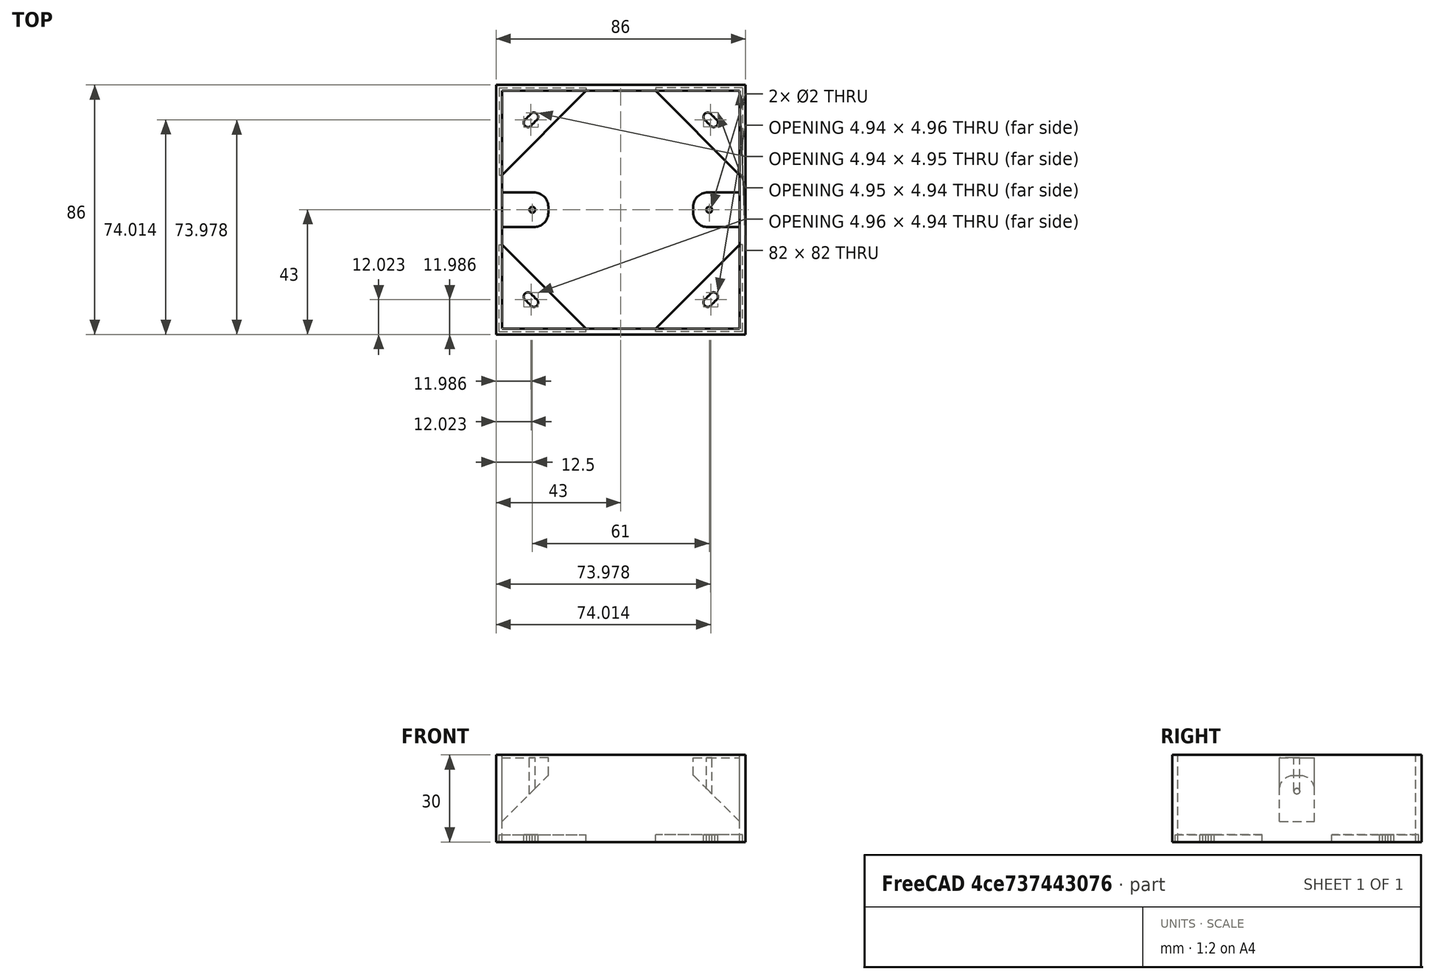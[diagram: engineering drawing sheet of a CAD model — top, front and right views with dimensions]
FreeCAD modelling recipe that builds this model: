
FCSTD DOCUMENT  (FreeCAD 0.16R)
Label: sonoff-aufputz-1v4
License: All rights reserved
LicenseURL: http://en.wikipedia.org/wiki/All_rights_reserved
objects: Part::Cut×19, Part::Cylinder×14, Part::Box×12, Part::Chamfer×6, Part::Fillet×2
note: 53 computed .brp shape members not serialized (recipe doc carries the construction recipe); baked Part::Feature solids carry a one-line shape summary decoded from their .brp

FEATURE [Part::Box] Box  label="Cube"
  Height = 30
  Length = 86
  Width = 86
FEATURE [Part::Box] Box001  label="Cube001"
  Height = 30
  Length = 82
  Placement = pos=(2,2,0) rot=(0,0,1;0rad)
  Width = 82
FEATURE [Part::Cut] Cut
  Base = -> Box
  Tool = -> Box001
FEATURE [Part::Box] Box002  label="Cube002"
  Height = 29
  Length = 16
  Placement = pos=(2,37,0) rot=(0,0,1;0rad)
  Width = 12
FEATURE [Part::Box] Box003  label="Cube003"
  Height = 29
  Length = 16
  Placement = pos=(68,37,0) rot=(0,0,1;0rad)
  Width = 12
FEATURE [Part::Fillet] Fillet  label="Aufnahme1"
  Base = -> Box002
  Edges = 2 edges r=5: [Edge5,Edge7]
FEATURE [Part::Fillet] Fillet001  label="Aufnahme2"
  Base = -> Box003
  Edges = 2 edges r=5: [Edge1,Edge3]
FEATURE [Part::Cylinder] Cylinder  label="Loch1"
  Angle = 360
  Height = 29
  Placement = pos=(12.5,43,0) rot=(0,0,1;0rad)
  Radius = 1
FEATURE [Part::Cylinder] Cylinder001  label="Loch2"
  Angle = 360
  Height = 29
  Placement = pos=(73.5,43,0) rot=(0,0,1;0rad)
  Radius = 1
FEATURE [Part::Cut] Cut001
  Base = -> Fillet
  Tool = -> Cylinder
FEATURE [Part::Cut] Cut002
  Base = -> Fillet001
  Tool = -> Cylinder001
FEATURE [Part::Box] Box009  label="Cube009"
  Height = 2.5
  Length = 30
  Placement = pos=(0,-40,0) rot=(0,0,1;0rad)
  Width = 30
FEATURE [Part::Chamfer] Chamfer004
  Base = -> Box009
  Edges = 1 edges r=29: [Edge7]
FEATURE [Part::Cylinder] Cylinder002  label="Cylinder"
  Angle = 360
  Height = 2.5
  Placement = pos=(10,-28,0) rot=(0,0,1;0rad)
  Radius = 1.5
FEATURE [Part::Cylinder] Cylinder003  label="Cylinder001"
  Angle = 360
  Height = 2.5
  Placement = pos=(11,-29,0) rot=(0,0,1;0rad)
  Radius = 1.5
FEATURE [Part::Cylinder] Cylinder004  label="Cylinder002"
  Angle = 360
  Height = 2.5
  Placement = pos=(12,-30,0) rot=(0,0,1;0rad)
  Radius = 1.5
FEATURE [Part::Cut] Cut003
  Base = -> Chamfer004
  Tool = -> Cylinder002
FEATURE [Part::Cut] Cut004
  Base = -> Cut003
  Tool = -> Cylinder003
FEATURE [Part::Cut] Cut005
  Base = -> Cut004
  Placement = pos=(45,1,0) rot=(0,0,1;1.5708rad)
  Tool = -> Cylinder004
FEATURE [Part::Box] Box010  label="Cube010"
  Height = 2.5
  Length = 30
  Placement = pos=(0,-40,0) rot=(0,0,1;0rad)
  Width = 30
FEATURE [Part::Chamfer] Chamfer005
  Base = -> Box010
  Edges = 1 edges r=29: [Edge7]
FEATURE [Part::Cylinder] Cylinder005  label="Cylinder014"
  Angle = 360
  Height = 2.5
  Placement = pos=(10,-28,0) rot=(0,0,1;0rad)
  Radius = 1.5
FEATURE [Part::Cylinder] Cylinder006  label="Cylinder015"
  Angle = 360
  Height = 2.5
  Placement = pos=(11,-29,0) rot=(0,0,1;0rad)
  Radius = 1.5
FEATURE [Part::Cylinder] Cylinder007  label="Cylinder005"
  Angle = 360
  Height = 2.5
  Placement = pos=(12,-30,0) rot=(0,0,1;0rad)
  Radius = 1.5
FEATURE [Part::Cut] Cut006
  Base = -> Chamfer005
  Tool = -> Cylinder005
FEATURE [Part::Cut] Cut007
  Base = -> Cut006
  Tool = -> Cylinder006
FEATURE [Part::Cut] Cut008
  Base = -> Cut007
  Placement = pos=(85,45,0) rot=(0,0,1;3.14159rad)
  Tool = -> Cylinder007
FEATURE [Part::Box] Box011  label="Cube011"
  Height = 2.5
  Length = 30
  Placement = pos=(0,-40,0) rot=(0,0,1;0rad)
  Width = 30
FEATURE [Part::Chamfer] Chamfer006
  Base = -> Box011
  Edges = 1 edges r=29: [Edge7]
FEATURE [Part::Cylinder] Cylinder008  label="Cylinder016"
  Angle = 360
  Height = 2.5
  Placement = pos=(10,-28,0) rot=(0,0,1;0rad)
  Radius = 1.5
FEATURE [Part::Cylinder] Cylinder009  label="Cylinder017"
  Angle = 360
  Height = 2.5
  Placement = pos=(11,-29,0) rot=(0,0,1;0rad)
  Radius = 1.5
FEATURE [Part::Cylinder] Cylinder010  label="Cylinder018"
  Angle = 360
  Height = 2.5
  Placement = pos=(12,-30,0) rot=(0,0,1;0rad)
  Radius = 1.5
FEATURE [Part::Cut] Cut009
  Base = -> Chamfer006
  Tool = -> Cylinder008
FEATURE [Part::Cut] Cut010
  Base = -> Cut009
  Tool = -> Cylinder009
FEATURE [Part::Cut] Cut011
  Base = -> Cut010
  Placement = pos=(41,85,0) rot=(0,0,-1;1.5708rad)
  Tool = -> Cylinder010
FEATURE [Part::Box] Box012  label="Cube012"
  Height = 2.5
  Length = 30
  Placement = pos=(0,-40,0) rot=(0,0,1;0rad)
  Width = 30
FEATURE [Part::Chamfer] Chamfer007
  Base = -> Box012
  Edges = 1 edges r=29: [Edge7]
FEATURE [Part::Cylinder] Cylinder011  label="Cylinder019"
  Angle = 360
  Height = 2.5
  Placement = pos=(10,-28,0) rot=(0,0,1;0rad)
  Radius = 1.5
FEATURE [Part::Cylinder] Cylinder012  label="Cylinder020"
  Angle = 360
  Height = 2.5
  Placement = pos=(11,-29,0) rot=(0,0,1;0rad)
  Radius = 1.5
FEATURE [Part::Cylinder] Cylinder013  label="Cylinder011"
  Angle = 360
  Height = 2.5
  Placement = pos=(12,-30,0) rot=(0,0,1;0rad)
  Radius = 1.5
FEATURE [Part::Cut] Cut012
  Base = -> Chamfer007
  Tool = -> Cylinder011
FEATURE [Part::Cut] Cut013
  Base = -> Cut012
  Tool = -> Cylinder012
FEATURE [Part::Cut] Cut014
  Base = -> Cut013
  Placement = pos=(1,41,0) rot=(0,0,1;0rad)
  Tool = -> Cylinder013
FEATURE [Part::Box] Box013  label="Cube013"
  Height = 21
  Length = 21
  Placement = pos=(1,37,5) rot=(0,0,1;0rad)
  Width = 12
FEATURE [Part::Chamfer] Chamfer
  Base = -> Box013
  Edges = 1 edges r=20: [Edge2]
FEATURE [Part::Box] Box014  label="Cube014"
  Height = 21
  Length = 21
  Placement = pos=(1,37,5) rot=(0,0,1;0rad)
  Width = 12
FEATURE [Part::Chamfer] Chamfer008
  Base = -> Box014
  Edges = 1 edges r=20: [Edge2]
  Placement = pos=(86,86,0) rot=(0,0,1;3.14159rad)
FEATURE [Part::Cut] Cut015
  Base = -> Cut001
  Tool = -> Chamfer
FEATURE [Part::Cut] Cut016
  Base = -> Cut002
  Tool = -> Chamfer008
FEATURE [Part::Box] Box015  label="Cube015"
  Height = 6
  Length = 16
  Placement = pos=(2,37,0) rot=(0,0,1;0rad)
  Width = 12
FEATURE [Part::Box] Box016  label="Cube016"
  Height = 6
  Length = 16
  Placement = pos=(68,37,0) rot=(0,0,1;0rad)
  Width = 12
FEATURE [Part::Cut] Cut017
  Base = -> Cut015
  Tool = -> Box015
FEATURE [Part::Cut] Cut018
  Base = -> Cut016
  Tool = -> Box016
